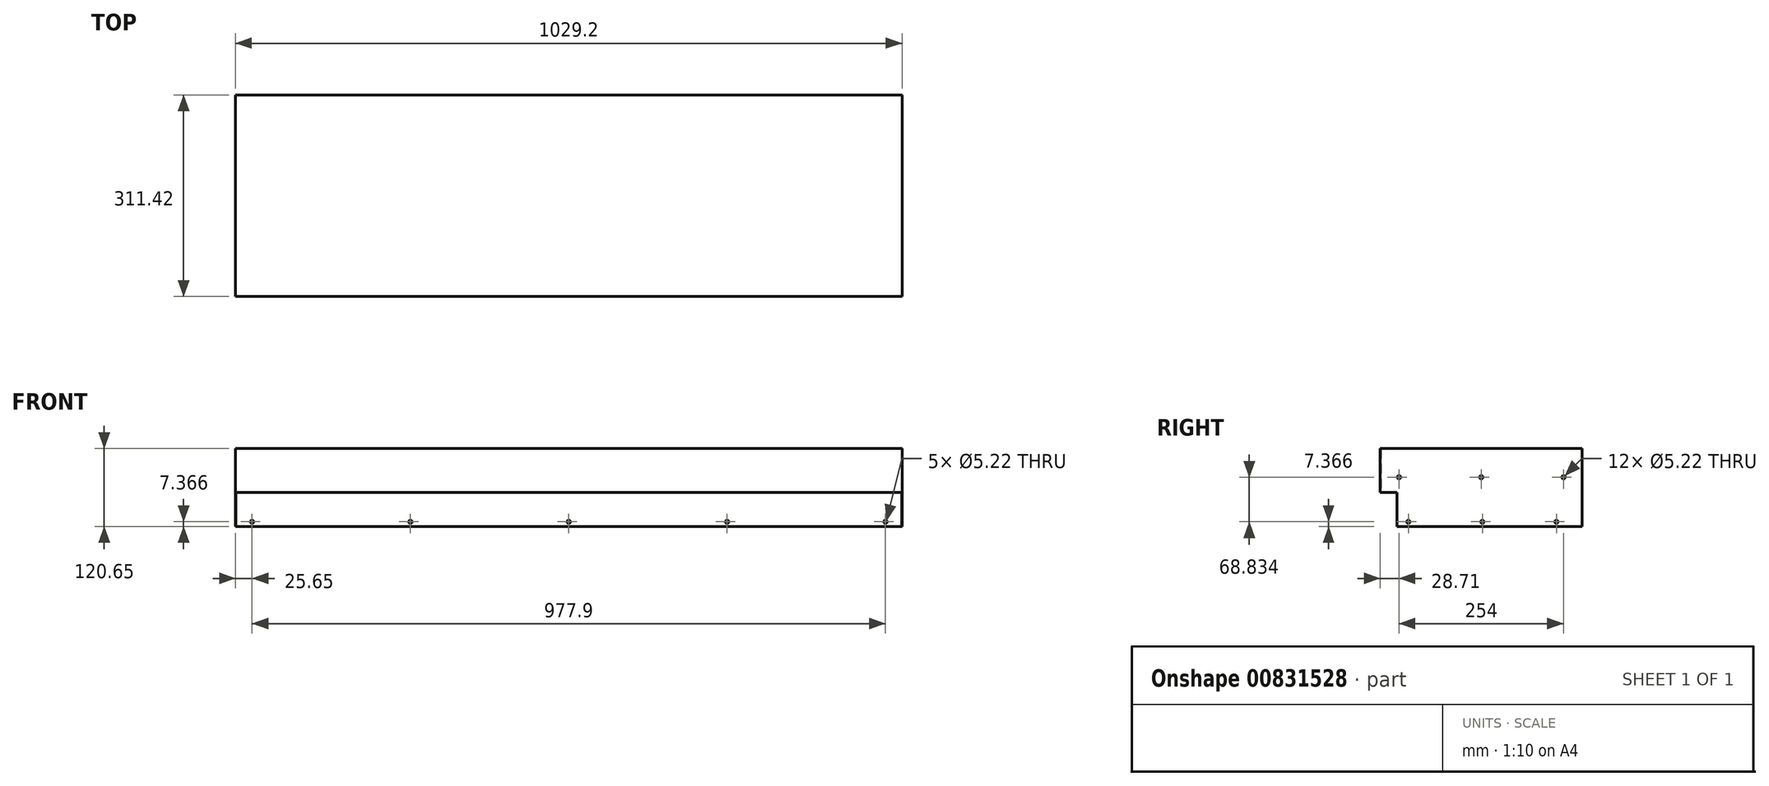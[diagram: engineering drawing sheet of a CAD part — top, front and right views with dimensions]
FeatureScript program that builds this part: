
annotation { "Feature Type Name" : "Feature", "Feature Type Description" : "" }
export const myFeature = defineFeature(function(context is Context, id is Id, definition is map)
    precondition{}
    {
        {
            var Q0;
            Q0=qCreatedBy(makeId("Top.planeOp"),FACE);
            var sketch = newSketch(context, id + "F0", { "sketchPlane" : qUnion([Q0])});
            skLineSegment(sketch, "E0.bottom", {"start": v(-514.6, 155.71) * mm, "end": v(514.6, 155.71) * mm});
            skLineSegment(sketch, "E0.top", {"start": v(-514.6, -155.71) * mm, "end": v(514.6, -155.71) * mm});
            skLineSegment(sketch, "E0.left", {"start": v(-514.6, 155.71) * mm, "end": v(-514.6, -155.71) * mm});
            skLineSegment(sketch, "E0.right", {"start": v(514.6, 155.71) * mm, "end": v(514.6, -155.71) * mm});
            skLineSegment(sketch, "E1", {"start": v(-514.6, 0) * mm, "end": v(0, 0) * mm, "construction": true});
            skLineSegment(sketch, "E2", {"start": v(0, 0) * mm, "end": v(0, 155.71) * mm, "construction": true});
            skSolve(sketch);
        }
        {
            var Q0;
            Q0=makeQuery(id+"F0.imprint","IMPRINT",FACE,{"disambiguationData":[TD([[makeQuery(id+"F0.imprint","IMPRINT",EDGE,{"derivedFrom":sQuery(id+"F0.wireOp",EDGE,"E0.bottom")}),-1.0]])]});
            extrude(context, id + "F1", {"entities" : qUnion([Q0]), "depth" : 120.65 * mm, "offsetDistance" : 25.4 * mm});
        }
        {
            var Q0;
            Q0=makeQuery(id+"F1.opExtrude","CAP_FACE",FACE,{"disambiguationData":[OSD([sQuery(id+"F0.wireOp",EDGE,"E0.bottom"),sQuery(id+"F0.wireOp",EDGE,"E0.top"),sQuery(id+"F0.wireOp",EDGE,"E0.left"),sQuery(id+"F0.wireOp",EDGE,"E0.right")])],"isStart":true});
            shell(context, id + "F2", {"entities" : qUnion([Q0]), "thickness" : 0.76 * mm});
        }
        {
            var Q0;
            Q0=makeQuery(id+"F1.opExtrude","SWEPT_FACE",FACE,{"disambiguationData":[OSD([sQuery(id+"F0.wireOp",EDGE,"E0.left")])]});
            var sketch = newSketch(context, id + "F3", { "sketchPlane" : qUnion([Q0])});
            skLineSegment(sketch, "E3.bottom", {"start": v(155.71, 0) * mm, "end": v(130.31, 0) * mm});
            skLineSegment(sketch, "E3.top", {"start": v(155.71, 52.58) * mm, "end": v(130.31, 52.58) * mm});
            skLineSegment(sketch, "E3.left", {"start": v(155.71, 0) * mm, "end": v(155.71, 52.58) * mm});
            skLineSegment(sketch, "E3.right", {"start": v(130.31, 0) * mm, "end": v(130.31, 52.58) * mm});
            skSolve(sketch);
        }
        {
            var Q0;
            Q0=makeQuery(id+"F3.imprint","IMPRINT",FACE,{"disambiguationData":[TD([[makeQuery(id+"F3.imprint","IMPRINT",EDGE,{"derivedFrom":sQuery(id+"F3.wireOp",EDGE,"E3.bottom")}),1.0]])]});
            extrude(context, id + "F4", {"entities" : qUnion([Q0]), "operationType" : NewBodyOperationType.REMOVE, "endBound" : BoundingType.THROUGH_ALL, "oppositeDirection" : true, "depth" : 25.4 * mm, "offsetDistance" : 25.4 * mm});
        }
        {
            var Q0;
            Q0=makeQuery(id+"F1.opExtrude","SWEPT_FACE",FACE,{"disambiguationData":[OSD([sQuery(id+"F0.wireOp",EDGE,"E0.bottom")])]});
            var sketch = newSketch(context, id + "F5", { "sketchPlane" : qUnion([Q0])});
            skPoint(sketch, "E4", {"position": v(-488.95, 7.37) * mm});
            skPoint(sketch, "E5", {"position": v(-244.47, 7.37) * mm});
            skPoint(sketch, "E6", {"position": v(244.47, 7.37) * mm});
            skPoint(sketch, "E7", {"position": v(488.95, 7.37) * mm});
            skLineSegment(sketch, "E8", {"start": v(-488.95, 7.37) * mm, "end": v(-244.47, 7.37) * mm});
            skLineSegment(sketch, "E9", {"start": v(244.47, 7.37) * mm, "end": v(488.95, 7.37) * mm});
            skLineSegment(sketch, "E10", {"start": v(-244.47, 7.37) * mm, "end": v(0, 7.37) * mm});
            skLineSegment(sketch, "E11", {"start": v(0, 7.37) * mm, "end": v(244.47, 7.37) * mm});
            skPoint(sketch, "E12", {"position": v(0, 7.37) * mm});
            skLineSegment(sketch, "E13", {"start": v(0, 0) * mm, "end": v(0, 7.37) * mm});
            skSolve(sketch);
        }
        {
            var Q0;
            Q0=sQuery(id+"F5.wireOp",VERTEX,"E4");
            var Q1;
            Q1=sQuery(id+"F5.wireOp",VERTEX,"f8e5c5c1-94b3-4a7b-a281-906d05fcf189");
            var Q2;
            Q2=sQuery(id+"F5.wireOp",VERTEX,"E7");
            var Q3;
            Q3=sQuery(id+"F5.wireOp",VERTEX,"E12");
            var Q4;
            Q4=sQuery(id+"F5.wireOp",VERTEX,"E5");
            var Q5;
            Q5=sQuery(id+"F5.wireOp",VERTEX,"E6");
            var Q6;
            Q6=makeQuery(id+"F1.opExtrude","SWEPT_BODY",BODY,{"disambiguationData":[OSD([sQuery(id+"F0.wireOp",EDGE,"E0.bottom"),sQuery(id+"F0.wireOp",EDGE,"E0.top"),sQuery(id+"F0.wireOp",EDGE,"E0.left"),sQuery(id+"F0.wireOp",EDGE,"E0.right")])]});
            hole(context, id + "F6", {"style" : HoleStyle.SIMPLE, "endStyle" : HoleEndStyle.BLIND, "standardTappedOrClearance" : lookupTablePath({ "standard" : "ANSI", "size" : "#5 (0.2)", "type" : "Drilled" }), "standardBlindInLast" : lookupTablePath({ "standard" : "ANSI", "size" : "#5 (0.2)", "type" : "Drilled" }), "holeDiameter" : 5.22 * mm, "majorDiameter" : 6.35 * mm, "holeDepth" : 1.02 * mm, "isTappedThrough" : true, "tappedDepth" : 12.7 * mm, "tapClearance" : 3, "locations" : qUnion([Q0, Q1, Q2, Q3, Q4, Q5]), "scope" : qUnion([Q6])});
        }
        {
            var Q0;
            Q0=makeQuery(id+"F1.opExtrude","SWEPT_FACE",FACE,{"disambiguationData":[OSD([sQuery(id+"F0.wireOp",EDGE,"E0.left")])]});
            var sketch = newSketch(context, id + "F7", { "sketchPlane" : qUnion([Q0])});
            skPoint(sketch, "E14", {"position": v(-116.1, 7.37) * mm});
            skPoint(sketch, "E15", {"position": v(-1.8, 7.37) * mm});
            skPoint(sketch, "E16", {"position": v(112.5, 7.37) * mm});
            skLineSegment(sketch, "E17", {"start": v(-116.1, 7.37) * mm, "end": v(-1.8, 7.37) * mm});
            skLineSegment(sketch, "E18", {"start": v(112.5, 7.37) * mm, "end": v(-1.8, 7.37) * mm});
            skSolve(sketch);
        }
        {
            var Q0;
            Q0=sQuery(id+"F7.wireOp",VERTEX,"E14");
            var Q1;
            Q1=sQuery(id+"F7.wireOp",VERTEX,"E15");
            var Q2;
            Q2=sQuery(id+"F7.wireOp",VERTEX,"E16");
            var Q3;
            Q3=makeQuery(id+"F1.opExtrude","SWEPT_BODY",BODY,{"disambiguationData":[OSD([sQuery(id+"F0.wireOp",EDGE,"E0.bottom"),sQuery(id+"F0.wireOp",EDGE,"E0.top"),sQuery(id+"F0.wireOp",EDGE,"E0.left"),sQuery(id+"F0.wireOp",EDGE,"E0.right")])]});
            hole(context, id + "F8", {"style" : HoleStyle.SIMPLE, "endStyle" : HoleEndStyle.THROUGH, "standardTappedOrClearance" : lookupTablePath({ "standard" : "ANSI", "size" : "#5 (0.2)", "type" : "Drilled" }), "standardBlindInLast" : lookupTablePath({ "standard" : "ANSI", "size" : "#5 (0.2)", "type" : "Drilled" }), "holeDiameter" : 5.22 * mm, "majorDiameter" : 6.35 * mm, "isTappedThrough" : true, "tappedDepth" : 12.7 * mm, "tapClearance" : 3, "locations" : qUnion([Q0, Q1, Q2]), "scope" : qUnion([Q3])});
        }
        {
            var Q0;
            Q0=makeQuery(id+"F1.opExtrude","SWEPT_FACE",FACE,{"disambiguationData":[OSD([sQuery(id+"F0.wireOp",EDGE,"E0.left")])]});
            var sketch = newSketch(context, id + "F9", { "sketchPlane" : qUnion([Q0])});
            skPoint(sketch, "E19", {"position": v(0, 76.2) * mm});
            skPoint(sketch, "E20", {"position": v(127, 76.2) * mm});
            skPoint(sketch, "E21", {"position": v(-127, 76.2) * mm});
            skLineSegment(sketch, "E22", {"start": v(127, 76.2) * mm, "end": v(0, 76.2) * mm});
            skLineSegment(sketch, "E23", {"start": v(-127, 76.2) * mm, "end": v(0, 76.2) * mm});
            skLineSegment(sketch, "E24", {"start": v(0, 76.2) * mm, "end": v(0, 120.65) * mm});
            skSolve(sketch);
        }
        {
            var Q0;
            Q0=sQuery(id+"F9.wireOp",VERTEX,"E21");
            var Q1;
            Q1=sQuery(id+"F9.wireOp",VERTEX,"E19");
            var Q2;
            Q2=sQuery(id+"F9.wireOp",VERTEX,"E20");
            var Q3;
            Q3=makeQuery(id+"F1.opExtrude","SWEPT_BODY",BODY,{"disambiguationData":[OSD([sQuery(id+"F0.wireOp",EDGE,"E0.bottom"),sQuery(id+"F0.wireOp",EDGE,"E0.top"),sQuery(id+"F0.wireOp",EDGE,"E0.left"),sQuery(id+"F0.wireOp",EDGE,"E0.right")])]});
            hole(context, id + "F10", {"style" : HoleStyle.SIMPLE, "endStyle" : HoleEndStyle.THROUGH, "standardTappedOrClearance" : lookupTablePath({ "standard" : "ANSI", "size" : "#5 (0.2)", "type" : "Drilled" }), "standardBlindInLast" : lookupTablePath({ "standard" : "ANSI", "size" : "#5 (0.2)", "type" : "Drilled" }), "holeDiameter" : 5.22 * mm, "majorDiameter" : 6.35 * mm, "isTappedThrough" : true, "tappedDepth" : 12.7 * mm, "tapClearance" : 3, "locations" : qUnion([Q0, Q1, Q2]), "scope" : qUnion([Q3])});
        }
    });
